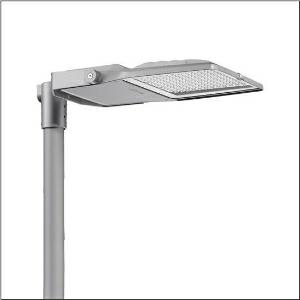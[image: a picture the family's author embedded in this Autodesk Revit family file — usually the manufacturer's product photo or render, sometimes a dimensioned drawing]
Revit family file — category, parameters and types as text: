
# Revit family: floodlight_fl_21_midi___pl43_5xa7786f4a3a_05ab
name_source: partatom
category: Lighting Fixtures
units: mm (PartAtom-declared; Revit-internal decimal feet)

## family parameters
Cut with Voids When Loaded = No
Host = Face
Light Source = No
Part Type = Normal
Room Calculation Point = No
Round Connector Dimension = Use Diameter
Shared = No

## types (1)
- --- (1 x LED, 38290 lm, 271.6 W, 4000K)
    Apparent Load = 272 VA
    CIE Flux Codes = 27 78 99 100 100
    Color Rendering = 70
    Color Temperature = 4000K
    Default Elevation = 1800 mm
    Description = Floodlight FL 21 midi, floodlight, primary light control with lens, of PMMA, primary optical cover: protective disc, of toughened safety glass, transparent, light distribution: PL43, light emission: direct distribution, installation type: surface-mounted, LED, High Power LED, rated luminous flux: 38.290lm, luminous efficacy: 141lm/W, light colour: 740, colour temperature: 4000K, control gear: Smart Interface (Zhaga)D4i, control: overheat protection, constant luminous flux control, time-dependent luminous flux control, flexible luminous flux parameterisation, pre-setting: logarithmic dimming characteristic, with terminal, 6-pole, mains connection: 220..240V, AC, 50/60Hz, start of lifetime: 272W, end of service life: 287W, reduction: 123W, mast bracket, of diecast aluminium, powder-coated, SITECO metallic grey (DB 702S), corrosivity category C5 mid according to DIN EN ISO 12944, suitable for swimming pools, chlorine-resistant, sealing non-destructively replaceable, mast bracket, of steel, galvanised, powder-coated, SITECO metallic grey (DB 702S), Smart Interface below and above, protection rating (complete): IP66, insulation class (complete): insulation class II (safety insulation), certification: CE, ENEC, VDE, protection symbol: D, impact resistance: IK08, permissible operating ambient temperature: -40..+40°C, permissible operating ambient temperature for outdoor applications: -40..+50°C, standard: DIN EN 12944, LABS conformity tested according to VDMA 24364:2018-05, packaging unit: 1 piece

Light Distribution: PL43
    Height = 76 mm
    Lamp = 1 x LED
    Lamp Light Flux = 38290 lm
    Lamp Power = 271.6 W
    Lamp count = 1
    Length = 657 mm
    Luminous efficacy = 141 lm/W
    Manufacturer = Siteco
    ModVariant = No
    Model = 5XA7786F4A3A
    Number of Poles = 1
    OnlyDefault = Yes
    Power Factor = 1
    Product Name = Floodlight FL 21 midi | PL43
    Product group = floodlight | pylon annexe
    ProductGroupID = 6201
    Protection Class = Protection class II
    Protection Degree = IP 66
    RLX_Detail_Level = 1
    RLX_Emergency_Light_Flux = 0 lm
    RLX_Emergency_Type = 0
    RLX_Emergency_Type_DB = No
    RlxData = <blob elided: 104453 chars, md5=47d9b588>
    Socket = socket
    Standby Power = 0 W
    System Light Flux = 38290 lm
    System Power = 272 W
    Type Comments = factory setting: luminous flux: 100 % | dim-lin: 254 | 620 mA
    Type Image = l_1007123.jpg
    URL = http://relux.com
    VarID = @adj_092993
    Voltage = 0 V
    Weight = 0.00 kg
    Width = 442 mm

## geometry (parser evidence)
native form markers: Blend x4, Sweep x11
no freeform markers — native parametric forms only
